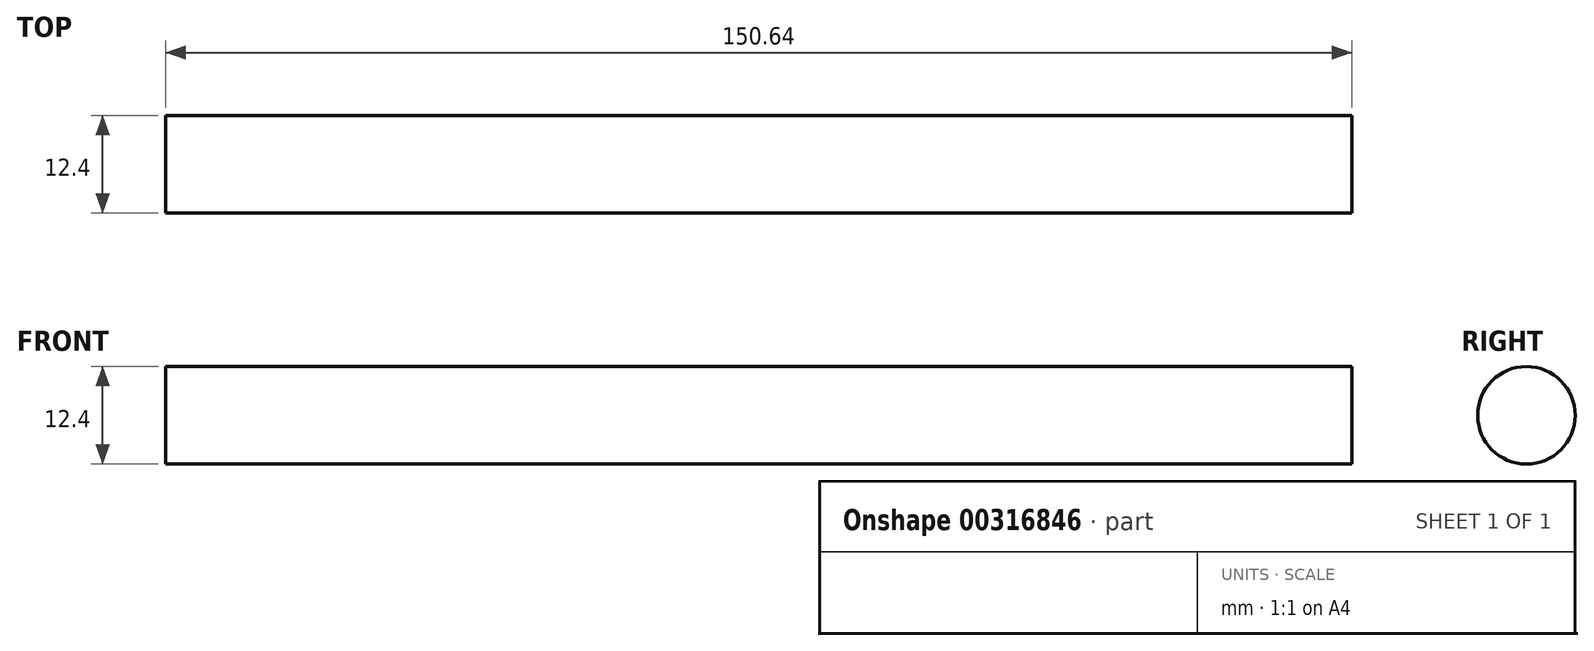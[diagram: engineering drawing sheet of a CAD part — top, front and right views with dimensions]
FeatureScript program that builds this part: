
annotation { "Feature Type Name" : "Feature", "Feature Type Description" : "" }
export const myFeature = defineFeature(function(context is Context, id is Id, definition is map)
    precondition{}
    {
        {
            var Q0;
            Q0=qCreatedBy(makeId("Front.planeOp"),FACE);
            var sketch = newSketch(context, id + "F0", { "sketchPlane" : qUnion([Q0])});
            skLineSegment(sketch, "E0", {"start": v(-75.32, 0.14) * mm, "end": v(75.32, 0.14) * mm});
            skCircle(sketch, "E1", {"center": v(0, 0) * mm, "radius": 4.61 * mm});
            skSolve(sketch);
        }
        {
            var Q0;
            Q0=qCreatedBy(makeId("Right.planeOp"),FACE);
            var sketch = newSketch(context, id + "F1", { "sketchPlane" : qUnion([Q0])});
            skCircle(sketch, "E2", {"center": v(0, 0) * mm, "radius": 6.2 * mm});
            skSolve(sketch);
        }
        {
            var Q0;
            Q0=makeQuery(id+"F1.imprint","IMPRINT",FACE,{"disambiguationData":[TD([[makeQuery(id+"F1.imprint","IMPRINT",EDGE,{"derivedFrom":sQuery(id+"F1.wireOp",EDGE,"E2")}),1.0]])]});
            var Q1;
            Q1=sQuery(id+"FkrYFAUEcVBqw92_0.wireOp",EDGE,"cjzd4ef0-PSUK-ESi2-IjZ5-vADDgGktoumE");
            var Q2;
            Q2=sQuery(id+"F0.wireOp",EDGE,"E0");
            sweep(context, id + "F2", {"profiles" : qUnion([Q0]), "surfaceProfiles" : qUnion([Q1]), "path" : qUnion([Q2]), "keepProfileOrientation" : true});
        }
    });
